# Revit family: Comfort_Window_B_Side_Hung_Standard
name_source: partatom
category: Windows
revit_build: Autodesk Revit 2014 (Build: 20130308_1515(x64)
units: mm (PartAtom-declared; Revit-internal decimal feet)

## types (6) — shared parameters
DG Gasket Thickness = 12 mm  [stored 0.0393701 ft]
Description = Comfort Window, Side Hung, Type B
Double Glazing Gasket Finish = Double Glazing Gasket Material
Frame Depth = 33 mm  [stored 0.108268 ft]
Frame Edge Thickness = 26 mm
Limit Fixed Pane Height Max = 1800 mm  [stored 5.90551 ft]
Limit Fixed Pane Height Min = 200 mm  [stored 0.656168 ft]
Limit Fixed Pane Width Max = 1800 mm  [stored 5.90551 ft]
Limit Fixed Pane Width Min = 200 mm  [stored 0.656168 ft]
Limit Sash Height Max = 1200 mm
Limit Sash Height Min = 300 mm  [stored 0.984252 ft]
Limit Sash Width Max = 600 mm  [stored 1.9685 ft]
Limit Sash Width Min = 300 mm  [stored 0.984252 ft]
Limit Window Height Max = 1275 mm  [stored 4.18307 ft]
Limit Window Height Min = 375 mm  [stored 1.23031 ft]
Manufacturer = Crealco
Max System DG One Piece Thickness = 4 mm  [stored 0.0131234 ft]
Max System DG Unit Thickness = 20 mm  [stored 0.0656168 ft]
Model = Comfort Window
Mullion Width = 27 mm  [stored 0.0885827 ft]
Rough Height = 590 mm  [stored 1.9357 ft]
Rough Width = 902 mm  [stored 2.95932 ft]
Sash Frame Gap = 5 mm  [stored 0.0164042 ft]
Sash Frame Side Gap = 12 mm  [stored 0.0393701 ft]
Sash Side Gap = 38 mm
Set Sash Width = 515 mm  [stored 1.68963 ft]
URL = http://www.crealco.co.za
zero-valued in all types: Visual Light Transmittance

## per-type parameters (varying)
| type | Clearvue SHGC Value | Clearvue U Value | Energy Advantage SHGC Value | Energy Advantage U Value | Intruderprufe LowE SHGC Value | Intruderprufe LowE U Value | Intruderprufe SHGC Value | Intruderprufe U Value | SmartGlass Elite SHGC Value | SmartGlass Elite U Value | SmartGlass Plus SHGC Value | SmartGlass Plus U Value | SmartGlass Standard SHGC Value | SmartGlass Standard U Value | SmartGlass Superior SHGC Value | SmartGlass Superior U Value | Window Height | Window Width |
| Comfort-0909S | 0.552 | 6.12 | 0.495 | 4.83 | 0.471 | 4.71 | 0.526 | 6.02 | 0.273 | 3.6 | 0.37 | 3.73 | 0.494 | 4.21 | 0.239 | 3.61 | 890 mm  [stored 2.91995 ft] | 890 mm  [stored 2.91995 ft] |
| Comfort-1209S | 0.605 | 6.07 | 0.542 | 4.63 | 0.513 | 4.51 | 0.575 | 5.97 | 0.296 | 3.26 | 0.402 | 3.41 | 0.539 | 3.95 | 0.258 | 3.26 | 890 mm  [stored 2.91995 ft] | 1190 mm  [stored 3.9042 ft] |
| Comfort-1509S | 0.637 | 6.05 | 0.571 | 4.51 | 0.538 | 4.4 | 0.604 | 5.94 | 0.309 | 3.05 | 0.421 | 3.21 | 0.566 | 3.79 | 0.269 | 3.06 | 890 mm  [stored 2.91995 ft] | 1490 mm  [stored 4.88845 ft] |
| Comfort-0912S | 0.575 | 6.1 | 0.516 | 4.75 | 0.489 | 4.63 | 0.548 | 6 | 0.283 | 3.46 | 0.384 | 3.6 | 0.514 | 4.1 | 0.247 | 3.47 | 1190 mm  [stored 3.9042 ft] | 890 mm  [stored 2.91995 ft] |
| Comfort-1212S | 0.628 | 6.06 | 0.563 | 4.55 | 0.531 | 4.43 | 0.596 | 5.95 | 0.305 | 3.12 | 0.416 | 3.27 | 0.559 | 3.84 | 0.266 | 3.12 | 1190 mm  [stored 3.9042 ft] | 1190 mm  [stored 3.9042 ft] |
| Comfort-1512S | 0.66 | 6.03 | 0.591 | 4.43 | 0.556 | 4.32 | 0.625 | 5.92 | 0.319 | 2.91 | 0.435 | 3.08 | 0.586 | 3.68 | 0.277 | 2.92 | 1190 mm  [stored 3.9042 ft] | 1490 mm  [stored 4.88845 ft] |

note: [stored X ft] marks values corroborated as IEEE doubles in the binary element streams (Revit-internal decimal feet)

## geometry (parser evidence)
native form markers: Sweep x15
no freeform markers — native parametric forms only
